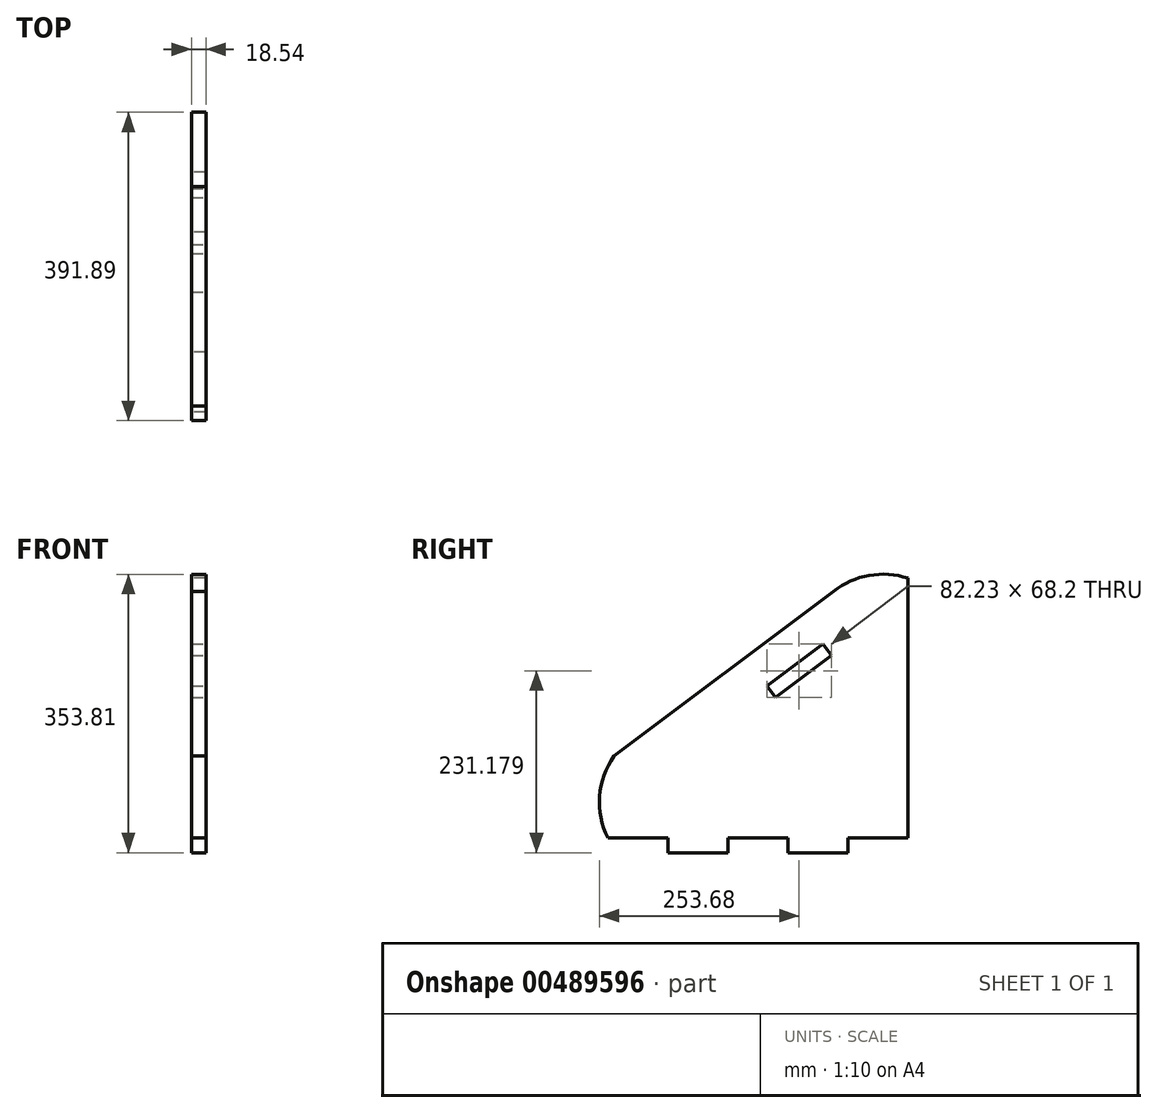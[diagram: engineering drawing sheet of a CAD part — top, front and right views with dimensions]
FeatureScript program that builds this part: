
annotation { "Feature Type Name" : "Feature", "Feature Type Description" : "" }
export const myFeature = defineFeature(function(context is Context, id is Id, definition is map)
    precondition{}
    {
        {
            var Q0;
            Q0=qCreatedBy(makeId("Right.planeOp"),FACE);
            var sketch = newSketch(context, id + "F0", { "sketchPlane" : qUnion([Q0])});
            skLineSegment(sketch, "E0", {"start": v(-207.24, 0) * mm, "end": v(173.76, 0) * mm});
            skLineSegment(sketch, "E1", {"start": v(173.76, 0) * mm, "end": v(173.76, 330.2) * mm});
            skArc(sketch, "E2", {"start": v(173.76, 330.2) * mm, "mid": v(124.46, 333.73) * mm, "end": v(79.33, 313.59) * mm});
            skArc(sketch, "E3", {"start": v(-199.65, 104.19) * mm, "mid": v(-217.86, 53.14) * mm, "end": v(-207.24, 0) * mm});
            skLineSegment(sketch, "E4", {"start": v(-199.65, 104.19) * mm, "end": v(79.33, 313.59) * mm});
            skSolve(sketch);
        }
        {
            var Q0;
            Q0 = qSketchRegion(id + "F0", true);
            extrude(context, id + "F1", {"entities" : qUnion([Q0]), "depth" : 18.54 * mm, "offsetDistance" : 25.4 * mm});
        }
        {
            var Q0;
            Q0=makeQuery(id+"F1.opExtrude","SWEPT_FACE",FACE,{"disambiguationData":[OSD([sQuery(id+"F0.wireOp",EDGE,"E0")])]});
            var sketch = newSketch(context, id + "F2", { "sketchPlane" : qUnion([Q0])});
            skLineSegment(sketch, "E5", {"start": v(18.54, 207.24) * mm, "end": v(18.54, 131.04) * mm});
            skLineSegment(sketch, "E6", {"start": v(18.54, 131.04) * mm, "end": v(18.54, 54.84) * mm});
            skLineSegment(sketch, "E7", {"start": v(18.54, 54.84) * mm, "end": v(18.54, -21.36) * mm});
            skLineSegment(sketch, "E8", {"start": v(18.54, -21.36) * mm, "end": v(18.54, -97.56) * mm});
            skLineSegment(sketch, "E9", {"start": v(18.54, -97.56) * mm, "end": v(18.54, -173.76) * mm});
            skLineSegment(sketch, "E10", {"start": v(18.54, 131.04) * mm, "end": v(0, 131.04) * mm});
            skLineSegment(sketch, "E11", {"start": v(0, 131.04) * mm, "end": v(0, 54.84) * mm});
            skLineSegment(sketch, "E12", {"start": v(0, 54.84) * mm, "end": v(18.54, 54.84) * mm});
            skLineSegment(sketch, "E13", {"start": v(18.54, -21.36) * mm, "end": v(0, -21.36) * mm});
            skLineSegment(sketch, "E14", {"start": v(18.54, -97.56) * mm, "end": v(0, -97.56) * mm});
            skLineSegment(sketch, "E15", {"start": v(0, -97.56) * mm, "end": v(0, -21.36) * mm});
            skSolve(sketch);
        }
        {
            var Q0;
            Q0 = qSketchRegion(id + "F2", true);
            extrude(context, id + "F3", {"entities" : qUnion([Q0]), "operationType" : NewBodyOperationType.ADD, "depth" : 18.54 * mm, "offsetDistance" : 25.4 * mm});
        }
        {
            var Q0;
            Q0=makeQuery(id+"F3.boolean.opBoolean","MERGE",FACE,{"derivedFrom":[makeQuery(id+"F1.opExtrude","CAP_FACE",FACE,{"disambiguationData":[OSD([sQuery(id+"F0.wireOp",EDGE,"E0"),sQuery(id+"F0.wireOp",EDGE,"E1"),sQuery(id+"F0.wireOp",EDGE,"E2"),sQuery(id+"F0.wireOp",EDGE,"E3"),sQuery(id+"F0.wireOp",EDGE,"E4")])],"isStart":false}),makeQuery(id+"F3.opExtrude","SWEPT_FACE",FACE,{"disambiguationData":[OSD([sQuery(id+"F2.wireOp",EDGE,"E6")])]}),makeQuery(id+"F3.opExtrude","SWEPT_FACE",FACE,{"disambiguationData":[OSD([sQuery(id+"F2.wireOp",EDGE,"E8")])]})]});
            var sketch = newSketch(context, id + "F4", { "sketchPlane" : qUnion([Q0])});
            skLineSegment(sketch, "E16", {"start": v(-137.6, 94.26) * mm, "end": v(-66.5, 147.63) * mm});
            skLineSegment(sketch, "E17", {"start": v(-137.6, 94.26) * mm, "end": v(-126.48, 79.43) * mm});
            skLineSegment(sketch, "E18", {"start": v(-126.48, 79.43) * mm, "end": v(-55.38, 132.8) * mm});
            skLineSegment(sketch, "E19", {"start": v(-66.5, 147.63) * mm, "end": v(-55.38, 132.8) * mm});
            skLineSegment(sketch, "E20", {"start": v(-60.94, 140.21) * mm, "end": v(0, 185.95) * mm, "construction": true});
            skLineSegment(sketch, "E21.MirrorCS", {"start": v(-55.38, 132.8) * mm, "end": v(-66.5, 147.63) * mm});
            skLineSegment(sketch, "E22.MirrorCS", {"start": v(-126.48, 79.43) * mm, "end": v(-137.6, 94.26) * mm});
            skLineSegment(sketch, "E23.MirrorCS", {"start": v(5.57, 178.54) * mm, "end": v(-5.57, 193.37) * mm});
            skLineSegment(sketch, "E24.MirrorCS", {"start": v(65.53, 246.74) * mm, "end": v(-5.57, 193.37) * mm});
            skLineSegment(sketch, "E25.MirrorCS", {"start": v(76.66, 231.9) * mm, "end": v(5.57, 178.54) * mm});
            skLineSegment(sketch, "E26.MirrorCS", {"start": v(76.66, 231.9) * mm, "end": v(65.53, 246.74) * mm});
            skPoint(sketch, "E27.start.orphan", {"position": v(-30.47, 163.08) * mm});
            skSolve(sketch);
        }
        {
            var Q0;
            Q0=makeQuery(id+"F4.imprint","IMPRINT",FACE,{"disambiguationData":[TD([[makeQuery(id+"F4.imprint","IMPRINT",EDGE,{"derivedFrom":sQuery(id+"F4.wireOp",EDGE,"E23.MirrorCS")}),-1.0]])]});
            var Q1;
            Q1=makeQuery(id+"F4.imprint","IMPRINT",FACE,{"disambiguationData":[TD([[makeQuery(id+"F4.imprint","IMPRINT",EDGE,{"derivedFrom":sQuery(id+"F4.wireOp",EDGE,"E22.MirrorCS")}),-1.0]])]});
            extrude(context, id + "F5", {"entities" : qUnion([Q0, Q1]), "operationType" : NewBodyOperationType.REMOVE, "oppositeDirection" : true, "depth" : 25.4 * mm, "offsetDistance" : 25.4 * mm});
        }
    });
